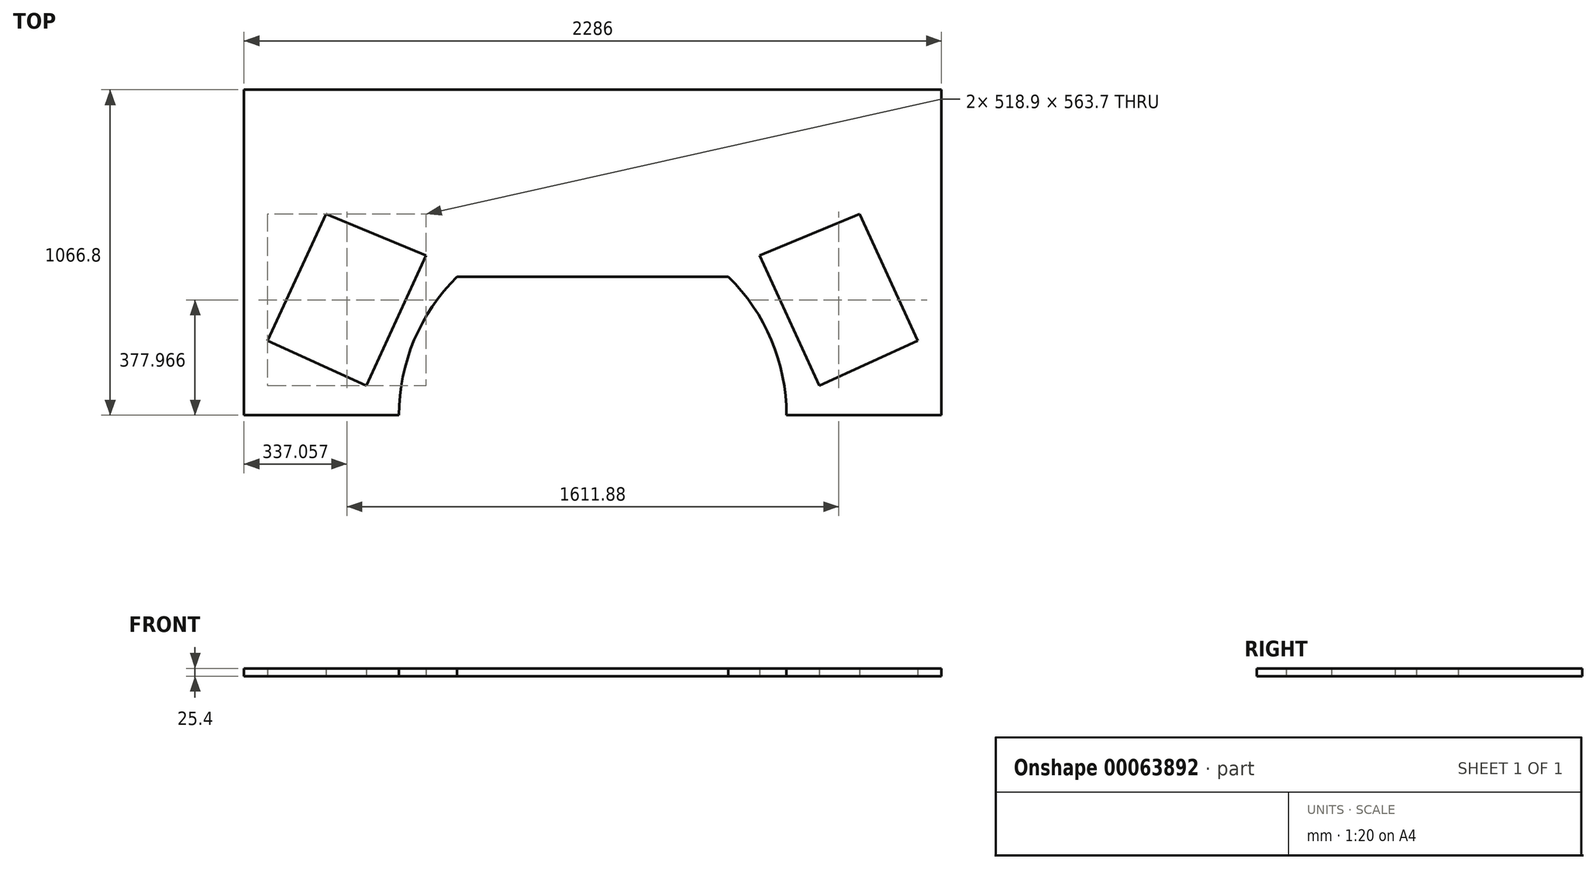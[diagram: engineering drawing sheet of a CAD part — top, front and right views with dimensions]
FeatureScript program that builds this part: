
annotation { "Feature Type Name" : "Feature", "Feature Type Description" : "" }
export const myFeature = defineFeature(function(context is Context, id is Id, definition is map)
    precondition{}
    {
        {
            var Q0;
            Q0=qCreatedBy(makeId("Top.planeOp"),FACE);
            var sketch = newSketch(context, id + "F0", { "sketchPlane" : qUnion([Q0])});
            skLineSegment(sketch, "E0.top", {"start": v(-1143, 609.6) * mm, "end": v(0, 609.6) * mm});
            skLineSegment(sketch, "E0.left", {"start": v(-1143, 0) * mm, "end": v(-1143, 609.6) * mm});
            skPoint(sketch, "E1.start.orphan", {"position": v(0, 177.8) * mm});
            skLineSegment(sketch, "E2", {"start": v(-1143, 0) * mm, "end": v(-1143, -457.2) * mm});
            skLineSegment(sketch, "E3", {"start": v(-1143, -457.2) * mm, "end": v(-635, -457.2) * mm});
            skLineSegment(sketch, "E4", {"start": v(-635, -457.2) * mm, "end": v(-635, -457.2) * mm});
            skArc(sketch, "E5", {"start": v(3.18, 177.8) * mm, "mid": v(0, 177.8) * mm, "end": v(-3.18, 177.8) * mm});
            skPoint(sketch, "E6.MirrorP", {"position": v(3.17, 177.64) * mm});
            skLineSegment(sketch, "E7.MirrorCS", {"start": v(634.96, -438.3) * mm, "end": v(634.96, -438.3) * mm});
            skLineSegment(sketch, "E8.MirrorCS", {"start": v(1135.13, -438.3) * mm, "end": v(1132.5, -438.3) * mm});
            skPoint(sketch, "E9.end.orphan", {"position": v(-585.44, -211.27) * mm});
            skPoint(sketch, "E10.orphan", {"position": v(-444.5, -3.72) * mm});
            skPoint(sketch, "E11.MirrorCS.end.orphan", {"position": v(0, 609.6) * mm});
            skLineSegment(sketch, "E12", {"start": v(0, 609.6) * mm, "end": v(0, -457.2) * mm, "construction": true});
            skLineSegment(sketch, "E13.MirrorCS", {"start": v(1143, 0) * mm, "end": v(1143, 609.6) * mm});
            skLineSegment(sketch, "E14.MirrorCS", {"start": v(1143, 0) * mm, "end": v(1143, -457.2) * mm});
            skLineSegment(sketch, "E15.MirrorCS", {"start": v(1143, -457.2) * mm, "end": v(635, -457.2) * mm});
            skArc(sketch, "E16.MirrorCS", {"start": v(-3.18, 177.8) * mm, "mid": v(0, 177.8) * mm, "end": v(3.18, 177.8) * mm});
            skPoint(sketch, "E17.MirrorP", {"position": v(-3.17, 177.64) * mm});
            skLineSegment(sketch, "E18.MirrorCS", {"start": v(1143, 609.6) * mm, "end": v(0, 609.6) * mm});
            skPoint(sketch, "E19.MirrorP", {"position": v(585.44, -211.27) * mm});
            skPoint(sketch, "E20.MirrorP", {"position": v(444.5, -3.72) * mm});
            skLineSegment(sketch, "E21", {"start": v(-444.5, -3.72) * mm, "end": v(444.5, -3.72) * mm});
            skArc(sketch, "E22.trimOffspring", {"start": v(-444.5, -3.72) * mm, "mid": v(-585.44, -211.27) * mm, "end": v(-635, -457.2) * mm});
            skArc(sketch, "E23.trimOffspring", {"start": v(444.5, -3.72) * mm, "mid": v(585.44, -211.27) * mm, "end": v(635, -457.2) * mm});
            skLineSegment(sketch, "E24", {"start": v(585.44, -211.27) * mm, "end": v(658.35, -177.84) * mm, "construction": true});
            skLineSegment(sketch, "E25", {"start": v(658.35, -177.84) * mm, "end": v(742.35, -361.09) * mm});
            skLineSegment(sketch, "E26", {"start": v(742.35, -361.09) * mm, "end": v(1065.4, -213) * mm});
            skLineSegment(sketch, "E27", {"start": v(1065.4, -213) * mm, "end": v(874.86, 202.62) * mm});
            skLineSegment(sketch, "E28", {"start": v(658.35, -177.84) * mm, "end": v(546.5, 66.15) * mm});
            skLineSegment(sketch, "E29", {"start": v(546.5, 66.15) * mm, "end": v(874.86, 202.62) * mm});
            skLineSegment(sketch, "E30.MirrorCS", {"start": v(-546.5, 66.15) * mm, "end": v(-874.86, 202.62) * mm});
            skLineSegment(sketch, "E31.MirrorCS", {"start": v(-658.35, -177.84) * mm, "end": v(-546.5, 66.15) * mm});
            skLineSegment(sketch, "E32.MirrorCS", {"start": v(-546.5, 66.15) * mm, "end": v(-742.35, -361.09) * mm});
            skLineSegment(sketch, "E33.MirrorCS", {"start": v(-742.35, -361.09) * mm, "end": v(-1065.4, -213) * mm});
            skLineSegment(sketch, "E34.MirrorCS", {"start": v(-1065.4, -213) * mm, "end": v(-874.86, 202.62) * mm});
            skPoint(sketch, "E35.orphan", {"position": v(-658.35, -177.84) * mm});
            skSolve(sketch);
        }
        {
            var Q0;
            Q0=makeQuery(id+"F0.imprint","IMPRINT",FACE,{"disambiguationData":[TD([[makeQuery(id+"F0.imprint","IMPRINT",EDGE,{"derivedFrom":sQuery(id+"F0.wireOp",EDGE,"E0.top")}),-1.0]])]});
            extrude(context, id + "F1", {"entities" : qUnion([Q0]), "depth" : 25.4 * mm});
        }
    });
